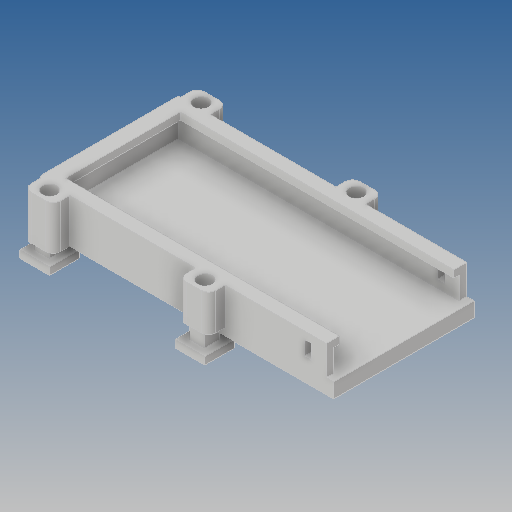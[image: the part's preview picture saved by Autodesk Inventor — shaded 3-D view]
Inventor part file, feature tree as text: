
AUTODESK INVENTOR PART (.ipt)
format: ipt  version: 2020 (Build 240168000, 168)  size: 318,464 bytes
history: native  units: mm
features: extrude x11, sketch x9, projected_geometry x3, fillet x2, other x1, pattern_linear x1, mirror x1
ambient origin geometry x8: Origin, YZ Plane, XZ Plane, XY Plane, X Axis, Y Axis, Z Axis, Center Point
bodies: Body1 (feature_tree)
feature tree (28):
  other  "Твердое тело1"
  sketch  "Эскиз1"
  extrude  "Выдавливание1"  Depth=38.0mm
  extrude  "Выдавливание2"  Depth=1.0mm TaperAngle=0.0deg
  extrude  "Выдавливание3"  Depth=3.0mm TaperAngle=0.0deg
  extrude  "Выдавливание4"  Depth=2.0mm
  extrude  "Выдавливание5"  Depth=2.0mm
  extrude  "Выдавливание7"  Depth=1.0mm TaperAngle=0.0deg
  fillet  "Сопряжение1"  Radius=1.0mm
  sketch  "Эскиз8"
  extrude  "Выдавливание8"  Depth=2.0mm
  extrude  "Выдавливание9"  Depth=2.0mm
  extrude  "Выдавливание10"  Depth=1.0mm
  pattern_linear  "Прямоуг.массив2"  Spacing1=1.0mm  [1 undecoded]
  mirror  "Зеркальное отражение2"
  fillet  "Сопряжение3"  Radius=1.0mm
  extrude  "Выдавливание11"  Depth=2.0mm
  extrude  "Выдавливание12"  Depth=1.0mm TaperAngle=0.0deg
  sketch  "Эскиз2"
  sketch  "Эскиз3"
  sketch  "Эскиз5"
  sketch  "Эскиз7"
  projected_geometry  "Спроецированная петля3"
  projected_geometry  "Спроецированная петля4"
  sketch  "Эскиз9"
  projected_geometry  "Спроецированная петля5"
  sketch  "Эскиз10"
  sketch  "Эскиз11"
note: 1 required parameter value undecoded (feature->parameter linkage not recoverable at this tier; creation-order binding heuristic only, values carry confidence <= 0.55)
